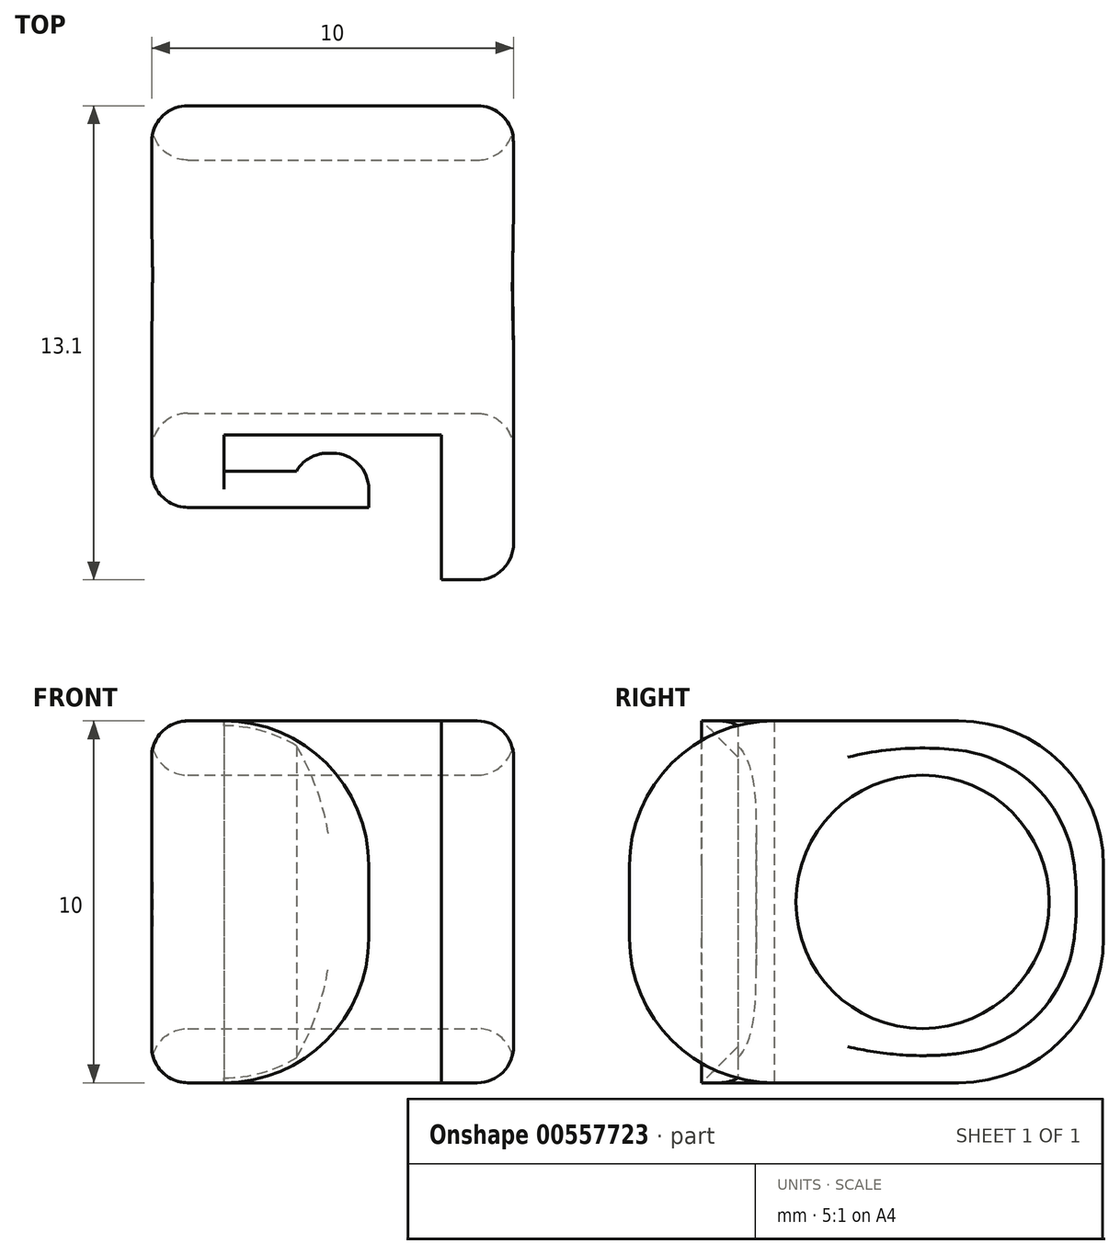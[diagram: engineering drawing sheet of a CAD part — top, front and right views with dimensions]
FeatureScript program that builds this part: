
annotation { "Feature Type Name" : "Feature", "Feature Type Description" : "" }
export const myFeature = defineFeature(function(context is Context, id is Id, definition is map)
    precondition{}
    {
        {
            var Q0;
            Q0=qCreatedBy(makeId("Top.planeOp"),FACE);
            var sketch = newSketch(context, id + "F0", { "sketchPlane" : qUnion([Q0])});
            skLineSegment(sketch, "E0", {"start": v(2, -1) * mm, "end": v(2, -2) * mm});
            skLineSegment(sketch, "E1", {"start": v(6, -1.5) * mm, "end": v(6, -3) * mm});
            skLineSegment(sketch, "E2", {"start": v(6, -3) * mm, "end": v(0, -3) * mm});
            skLineSegment(sketch, "E3", {"start": v(0, -3) * mm, "end": v(0, 0) * mm});
            skLineSegment(sketch, "E4", {"start": v(0, 0) * mm, "end": v(0, 0) * mm});
            skLineSegment(sketch, "E5", {"start": v(0, 0) * mm, "end": v(0, 8.1) * mm});
            skLineSegment(sketch, "E6", {"start": v(0, 8.1) * mm, "end": v(10, 8.1) * mm});
            skLineSegment(sketch, "E7", {"start": v(10, 8.1) * mm, "end": v(10, 0) * mm});
            skLineSegment(sketch, "E8", {"start": v(5, -1) * mm, "end": v(2, -1) * mm});
            skLineSegment(sketch, "E9", {"start": v(2, -2) * mm, "end": v(4, -2) * mm});
            skLineSegment(sketch, "E10", {"start": v(4, -2) * mm, "end": v(4, -1.5) * mm});
            skLineSegment(sketch, "E11", {"start": v(4, -1.5) * mm, "end": v(6, -1.5) * mm});
            skLineSegment(sketch, "E12", {"start": v(10, 0) * mm, "end": v(10, 0) * mm});
            skLineSegment(sketch, "E13", {"start": v(10, 0) * mm, "end": v(10, -5) * mm});
            skLineSegment(sketch, "E14", {"start": v(10, -5) * mm, "end": v(8, -5) * mm});
            skLineSegment(sketch, "E15", {"start": v(8, -5) * mm, "end": v(8, -1) * mm});
            skLineSegment(sketch, "E16", {"start": v(8, -1) * mm, "end": v(5, -1) * mm});
            skSolve(sketch);
        }
        {
            var Q0;
            Q0=makeQuery(id+"F0.imprint","IMPRINT",FACE,{"disambiguationData":[TD([[makeQuery(id+"F0.imprint","IMPRINT",EDGE,{"derivedFrom":sQuery(id+"F0.wireOp",EDGE,"E0")}),-1.0]])]});
            extrude(context, id + "F1", {"entities" : qUnion([Q0]), "endBound" : BoundingType.SYMMETRIC, "depth" : 10 * mm, "offsetDistance" : 25 * mm});
        }
        {
            var Q0;
            Q0=makeQuery(id+"F1.opExtrude","SWEPT_FACE",FACE,{"disambiguationData":[OSD([sQuery(id+"F0.wireOp",EDGE,"E7"),sQuery(id+"F0.wireOp",EDGE,"1kXGVvJr-JPgg-7YMV-aefA-PGxPgHNlz1uc")])]});
            var sketch = newSketch(context, id + "F2", { "sketchPlane" : qUnion([Q0])});
            skCircle(sketch, "E17", {"center": v(3.1, 0) * mm, "radius": 3.5 * mm});
            skLineSegment(sketch, "E18", {"start": v(8.1, 0) * mm, "end": v(3.1, 0) * mm, "construction": true});
            skSolve(sketch);
        }
        {
            var Q0;
            Q0=makeQuery(id+"F2.imprint","IMPRINT",FACE,{"disambiguationData":[TD([[makeQuery(id+"F2.imprint","IMPRINT",EDGE,{"derivedFrom":sQuery(id+"F2.wireOp",EDGE,"E17")}),1.0]])]});
            extrude(context, id + "F3", {"entities" : qUnion([Q0]), "operationType" : NewBodyOperationType.REMOVE, "endBound" : BoundingType.SYMMETRIC, "oppositeDirection" : true, "depth" : 25 * mm, "offsetDistance" : 25 * mm});
        }
        {
            var Q0;
            Q0=makeQuery(id+"F1.opExtrude","CAP_EDGE",EDGE,{"disambiguationData":[OSD([sQuery(id+"F0.wireOp",EDGE,"E6")])],"isStart":true});
            var Q1;
            Q1=makeQuery(id+"F1.opExtrude","CAP_EDGE",EDGE,{"disambiguationData":[OSD([sQuery(id+"F0.wireOp",EDGE,"E6")])],"isStart":false});
            var Q2;
            Q2=makeQuery(id+"F1.opExtrude","CAP_EDGE",EDGE,{"disambiguationData":[OSD([sQuery(id+"F0.wireOp",EDGE,"E14")])],"isStart":true});
            var Q3;
            Q3=makeQuery(id+"F1.opExtrude","CAP_EDGE",EDGE,{"disambiguationData":[OSD([sQuery(id+"F0.wireOp",EDGE,"E14")])],"isStart":false});
            var Q4;
            Q4=makeQuery(id+"F1.opExtrude","CAP_EDGE",EDGE,{"disambiguationData":[OSD([sQuery(id+"F0.wireOp",EDGE,"E1")])],"isStart":false});
            var Q5;
            Q5=makeQuery(id+"F1.opExtrude","CAP_EDGE",EDGE,{"disambiguationData":[OSD([sQuery(id+"F0.wireOp",EDGE,"E1")])],"isStart":true});
            fillet(context, id + "F4", {"entities" : qUnion([Q0, Q1, Q2, Q3, Q4, Q5]), "radius" : 4 * mm, "tangentPropagation" : true, "allowEdgeOverflow" : false});
        }
        {
            var Q0;
            Q0=makeQuery(id+"F1.opExtrude","CAP_EDGE",EDGE,{"disambiguationData":[OSD([sQuery(id+"F0.wireOp",EDGE,"E3")])],"isStart":false});
            var Q1;
            Q1=makeQuery(id+"F1.opExtrude","CAP_EDGE",EDGE,{"disambiguationData":[OSD([sQuery(id+"F0.wireOp",EDGE,"E3")])],"isStart":true});
            var Q2;
            Q2=makeQuery(id+"F1.opExtrude","SWEPT_FACE",FACE,{"disambiguationData":[OSD([sQuery(id+"F0.wireOp",EDGE,"E3")])]});
            var Q3;
            Q3=makeQuery(id+"F1.opExtrude","SWEPT_FACE",FACE,{"disambiguationData":[OSD([sQuery(id+"F0.wireOp",EDGE,"E13")])]});
            var Q4;
            Q4=makeQuery(id+"F1.opExtrude","SWEPT_EDGE",EDGE,{"disambiguationData":[OSD([sQuery(id+"F0.wireOp",EDGE,"E10"),sQuery(id+"F0.wireOp",EDGE,"E11")])]});
            var Q5;
            Q5=makeQuery(id+"F1.opExtrude","SWEPT_EDGE",EDGE,{"disambiguationData":[OSD([sQuery(id+"F0.wireOp",EDGE,"E1"),sQuery(id+"F0.wireOp",EDGE,"E11")])]});
            fillet(context, id + "F5", {"entities" : qUnion([Q0, Q1, Q2, Q3, Q4, Q5]), "radius" : 1 * mm, "tangentPropagation" : true, "allowEdgeOverflow" : false});
        }
    });
